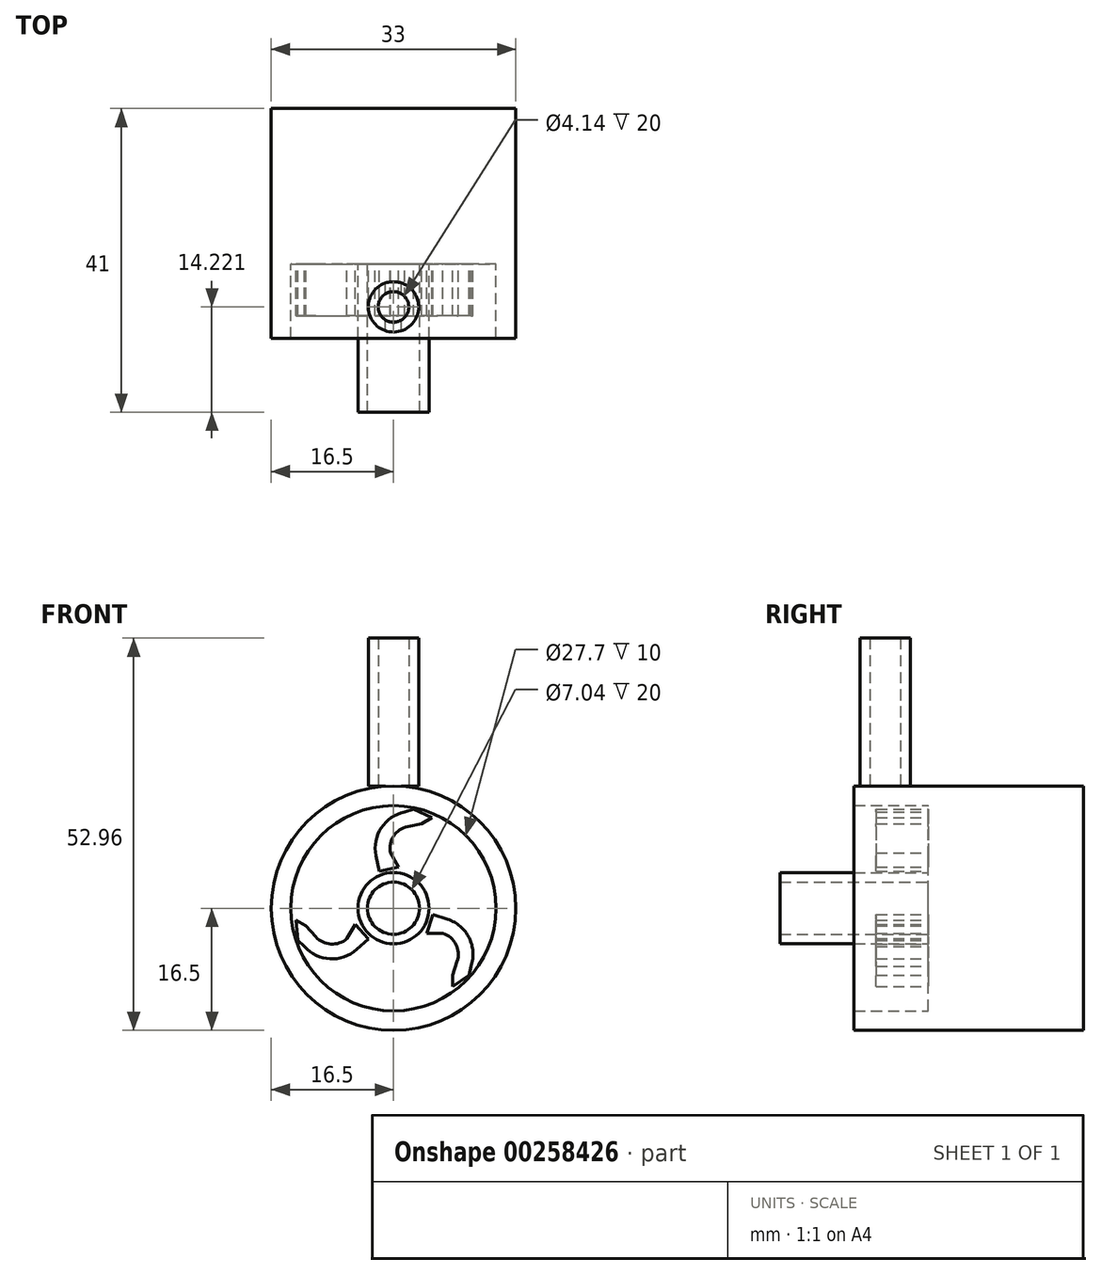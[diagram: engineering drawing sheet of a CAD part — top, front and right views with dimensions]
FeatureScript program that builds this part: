
annotation { "Feature Type Name" : "Feature", "Feature Type Description" : "" }
export const myFeature = defineFeature(function(context is Context, id is Id, definition is map)
    precondition{}
    {
        {
            var Q0;
            Q0=qCreatedBy(makeId("Front.planeOp"),FACE);
            var sketch = newSketch(context, id + "F0", { "sketchPlane" : qUnion([Q0])});
            skCircle(sketch, "E0", {"center": v(0, 0) * mm, "radius": 16.5 * mm});
            skSolve(sketch);
        }
        {
            var Q0;
            Q0 = qSketchRegion(id + "F0", true);
            extrude(context, id + "F1", {"entities" : qUnion([Q0]), "depth" : 21 * mm});
        }
        {
            var Q0;
            Q0=makeQuery(id+"F1.opExtrude","CAP_FACE",FACE,{"disambiguationData":[OSD([sQuery(id+"F0.wireOp",EDGE,"E0")])],"isStart":false});
            var sketch = newSketch(context, id + "F2", { "sketchPlane" : qUnion([Q0])});
            skCircle(sketch, "E1", {"center": v(0, 0) * mm, "radius": 16.5 * mm});
            skCircle(sketch, "E2", {"center": v(0, 0) * mm, "radius": 13.85 * mm});
            skSolve(sketch);
        }
        {
            var Q0;
            Q0=makeQuery(id+"F2.imprint","IMPRINT",FACE,{"disambiguationData":[TD([[makeQuery(id+"F2.imprint","IMPRINT",EDGE,{"derivedFrom":sQuery(id+"F2.wireOp",EDGE,"E1")}),1.0]])]});
            extrude(context, id + "F3", {"entities" : qUnion([Q0]), "operationType" : NewBodyOperationType.ADD, "depth" : 10 * mm});
        }
        {
            var Q0;
            Q0=makeQuery(id+"F1.opExtrude","CAP_FACE",FACE,{"disambiguationData":[OSD([sQuery(id+"F0.wireOp",EDGE,"E0")])],"isStart":false});
            var sketch = newSketch(context, id + "F4", { "sketchPlane" : qUnion([Q0])});
            skCircle(sketch, "E3", {"center": v(0, 0) * mm, "radius": 4.8 * mm});
            skCircle(sketch, "E4", {"center": v(0, 0) * mm, "radius": 3.52 * mm});
            skSolve(sketch);
        }
        {
            var Q0;
            Q0 = qSketchRegion(id + "F4", true);
            extrude(context, id + "F5", {"entities" : qUnion([Q0]), "operationType" : NewBodyOperationType.ADD, "depth" : 20 * mm});
        }
        {
            var Q0;
            Q0=makeQuery(id+"F5.boolean.opBoolean","SPLIT",FACE,{"disambiguationData":[TD([makeQuery(id+"F3.opExtrude","SWEPT_FACE",FACE,{"disambiguationData":[OSD([sQuery(id+"F2.wireOp",EDGE,"E2")])]})])],"derivedFrom":makeQuery(id+"F1.opExtrude","CAP_FACE",FACE,{"disambiguationData":[OSD([sQuery(id+"F0.wireOp",EDGE,"E0")])],"isStart":false})});
            var sketch = newSketch(context, id + "F6", { "sketchPlane" : qUnion([Q0])});
            skPoint(sketch, "E5.visualSharp", {"position": v(12.06, -3.07) * mm});
            skArc(sketch, "E5.filletArc", {"start": v(10.49, -7.81) * mm, "mid": v(10.2, -4) * mm, "end": v(7.31, -1.5) * mm});
            skArc(sketch, "E6.1", {"start": v(8.59, -7.18) * mm, "mid": v(8.42, -4.9) * mm, "end": v(6.68, -3.4) * mm});
            skLineSegment(sketch, "E6.2", {"start": v(8.59, -7.18) * mm, "end": v(7.98, -9.02) * mm});
            skPoint(sketch, "E7.center", {"position": v(0, 0) * mm});
            skLineSegment(sketch, "E8", {"start": v(7.31, -1.5) * mm, "end": v(5.31, -0.83) * mm});
            skLineSegment(sketch, "E9", {"start": v(5.31, -0.83) * mm, "end": v(4.47, -3.4) * mm});
            skLineSegment(sketch, "E10", {"start": v(4.47, -3.4) * mm, "end": v(6.68, -3.4) * mm});
            skLineSegment(sketch, "E11", {"start": v(10.49, -7.81) * mm, "end": v(10.2, -9.02) * mm});
            skPoint(sketch, "E11.endSnap0", {"position": v(10.2, -4) * mm});
            skLineSegment(sketch, "E12", {"start": v(10.2, -9.02) * mm, "end": v(7.98, -10.59) * mm});
            skLineSegment(sketch, "E13", {"start": v(7.98, -10.59) * mm, "end": v(7.98, -9.02) * mm});
            skLineSegment(sketch, "E14.1.0", {"start": v(-2.36, 7.08) * mm, "end": v(-1.94, 5.02) * mm});
            skLineSegment(sketch, "E14.1.1", {"start": v(-1.94, 5.02) * mm, "end": v(0.7, 5.56) * mm});
            skLineSegment(sketch, "E14.1.2", {"start": v(0.7, 5.56) * mm, "end": v(-0.4, 7.48) * mm});
            skArc(sketch, "E14.1.3", {"start": v(1.93, 11.03) * mm, "mid": v(0.03, 9.74) * mm, "end": v(-0.4, 7.48) * mm});
            skLineSegment(sketch, "E14.1.4", {"start": v(1.93, 11.03) * mm, "end": v(3.82, 11.42) * mm});
            skLineSegment(sketch, "E14.1.5", {"start": v(5.18, 12.2) * mm, "end": v(3.82, 11.42) * mm});
            skLineSegment(sketch, "E14.1.6", {"start": v(2.7, 13.35) * mm, "end": v(5.18, 12.2) * mm});
            skLineSegment(sketch, "E14.1.7", {"start": v(1.52, 12.99) * mm, "end": v(2.7, 13.35) * mm});
            skArc(sketch, "E14.1.8", {"start": v(1.52, 12.99) * mm, "mid": v(-1.64, 10.84) * mm, "end": v(-2.36, 7.08) * mm});
            skLineSegment(sketch, "E14.2.0", {"start": v(-4.95, -5.58) * mm, "end": v(-3.38, -4.19) * mm});
            skLineSegment(sketch, "E14.2.1", {"start": v(-3.38, -4.19) * mm, "end": v(-5.17, -2.17) * mm});
            skLineSegment(sketch, "E14.2.2", {"start": v(-5.17, -2.17) * mm, "end": v(-6.28, -4.1) * mm});
            skArc(sketch, "E14.2.3", {"start": v(-10.52, -3.84) * mm, "mid": v(-8.45, -4.84) * mm, "end": v(-6.28, -4.1) * mm});
            skLineSegment(sketch, "E14.2.4", {"start": v(-10.52, -3.84) * mm, "end": v(-11.8, -2.4) * mm});
            skLineSegment(sketch, "E14.2.5", {"start": v(-13.16, -1.62) * mm, "end": v(-11.8, -2.4) * mm});
            skLineSegment(sketch, "E14.2.6", {"start": v(-12.91, -4.33) * mm, "end": v(-13.16, -1.62) * mm});
            skLineSegment(sketch, "E14.2.7", {"start": v(-12, -5.17) * mm, "end": v(-12.91, -4.33) * mm});
            skArc(sketch, "E14.2.8", {"start": v(-12, -5.17) * mm, "mid": v(-8.56, -6.84) * mm, "end": v(-4.95, -5.58) * mm});
            skSolve(sketch);
        }
        {
            var Q0;
            Q0 = qSketchRegion(id + "F6", true);
            extrude(context, id + "F7", {"entities" : qUnion([Q0]), "operationType" : NewBodyOperationType.ADD, "depth" : 7 * mm});
        }
        {
            var Q0;
            Q0=qCreatedBy(makeId("Front.planeOp"),FACE);
            var sketch = newSketch(context, id + "F8", { "sketchPlane" : qUnion([Q0])});
            skPoint(sketch, "E15", {"position": v(0, 16.46) * mm});
            skSolve(sketch);
        }
        {
            var Q0;
            Q0=qCreatedBy(makeId("Top.planeOp"),FACE);
            var Q1;
            Q1=sQuery(id+"F8.wireOp",VERTEX,"E15");
            cPlane(context, id + "F9", {"entities" : qUnion([Q0, Q1]), "cplaneType" : CPlaneType.PLANE_POINT, "offset" : 25 * mm, "width" : 150 * mm, "height" : 150 * mm});
        }
        {
            var Q0;
            Q0=qCreatedBy(id+"F9.planeOp",FACE);
            var sketch = newSketch(context, id + "F10", { "sketchPlane" : qUnion([Q0])});
            skCircle(sketch, "E16", {"center": v(0, -26.78) * mm, "radius": 3.4 * mm});
            skCircle(sketch, "E17", {"center": v(0, -26.78) * mm, "radius": 2.07 * mm});
            skSolve(sketch);
        }
        {
            var Q0;
            Q0 = qSketchRegion(id + "F10", true);
            extrude(context, id + "F11", {"entities" : qUnion([Q0]), "operationType" : NewBodyOperationType.ADD, "depth" : 20 * mm});
        }
    });
